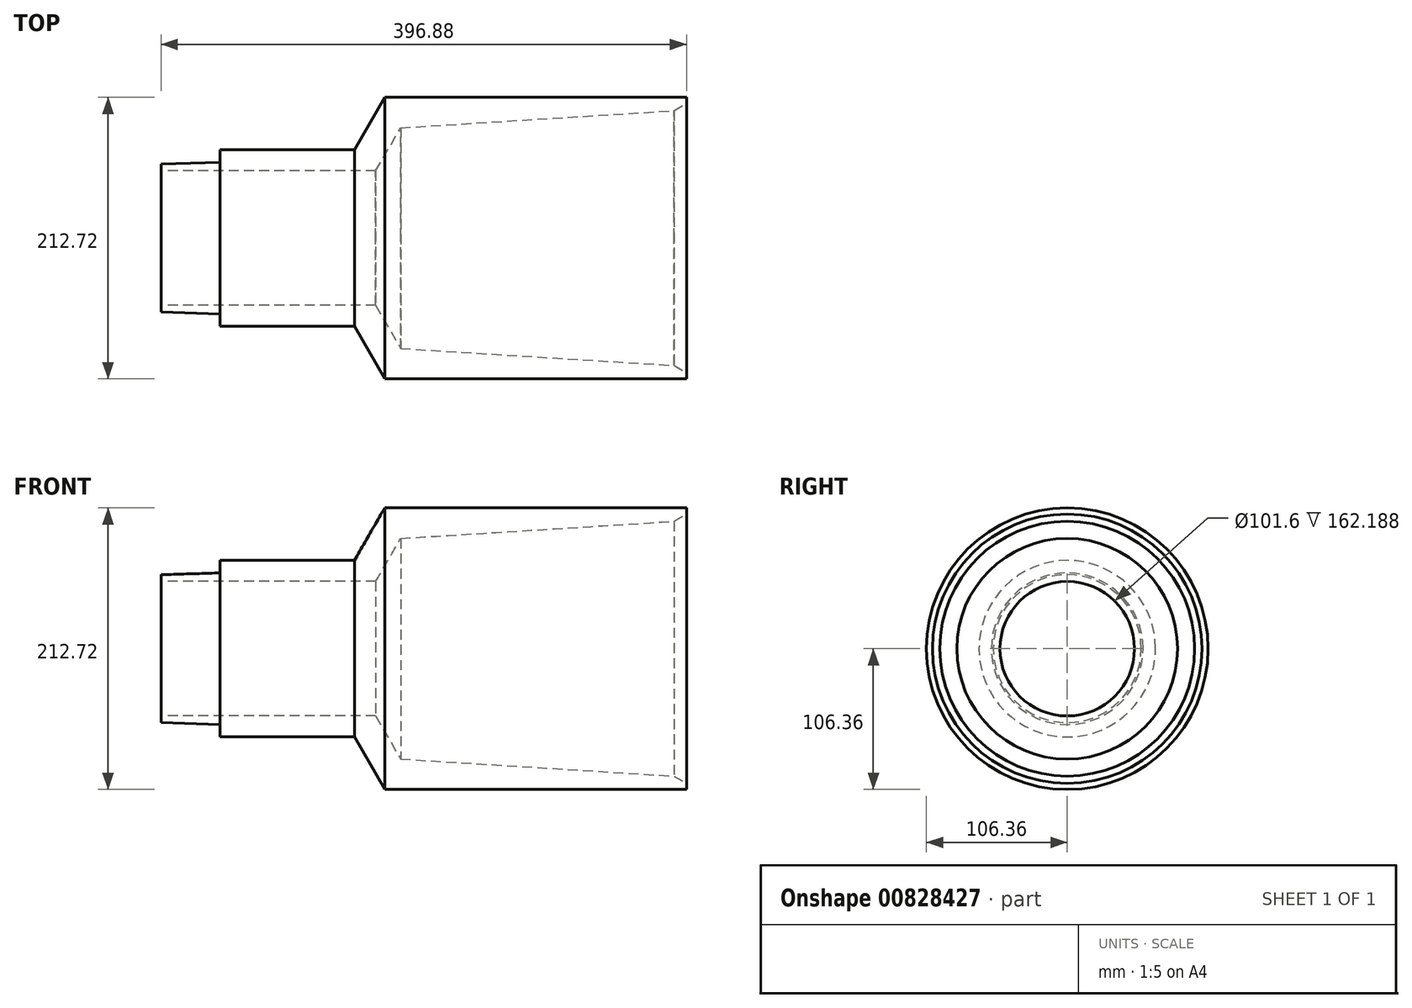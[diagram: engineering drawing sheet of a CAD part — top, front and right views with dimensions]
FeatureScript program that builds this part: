
annotation { "Feature Type Name" : "Feature", "Feature Type Description" : "" }
export const myFeature = defineFeature(function(context is Context, id is Id, definition is map)
    precondition{}
    {
        {
            var Q0;
            Q0=qCreatedBy(makeId("Front.planeOp"),FACE);
            var sketch = newSketch(context, id + "F0", { "sketchPlane" : qUnion([Q0])});
            skLineSegment(sketch, "E0", {"start": v(0, 50.8) * mm, "end": v(162.19, 50.8) * mm});
            skLineSegment(sketch, "E1", {"start": v(44.45, 66.68) * mm, "end": v(146.05, 66.68) * mm});
            skLineSegment(sketch, "E2", {"start": v(44.45, 66.68) * mm, "end": v(44.45, 57.28) * mm});
            skLineSegment(sketch, "E3", {"start": v(0, 55.89) * mm, "end": v(0, 50.8) * mm});
            skLineSegment(sketch, "E4", {"start": v(44.45, 57.28) * mm, "end": v(0, 55.89) * mm});
            skLineSegment(sketch, "E5", {"start": v(396.88, 106.36) * mm, "end": v(396.88, 101.74) * mm});
            skLineSegment(sketch, "E6", {"start": v(168.96, 106.36) * mm, "end": v(396.88, 106.36) * mm});
            skLineSegment(sketch, "E7", {"start": v(387.35, 96.24) * mm, "end": v(180.98, 83.34) * mm});
            skLineSegment(sketch, "E8", {"start": v(168.96, 106.36) * mm, "end": v(146.05, 66.68) * mm});
            skLineSegment(sketch, "E9", {"start": v(180.98, 83.34) * mm, "end": v(162.19, 50.8) * mm});
            skLineSegment(sketch, "E10", {"start": v(387.35, 96.24) * mm, "end": v(396.88, 101.74) * mm});
            skLineSegment(sketch, "E11", {"start": v(0, 0) * mm, "end": v(23.8, 0) * mm, "construction": true});
            skSolve(sketch);
        }
        {
            var Q0;
            Q0 = qSketchRegion(id + "F0", true);
            var Q1;
            Q1=sQuery(id+"F0.wireOp",EDGE,"E11");
            revolve(context, id + "F1", {"surfaceOperationType" : NewSurfaceOperationType.NEW, "entities" : qUnion([Q0]), "axis" : qUnion([Q1]), "revolveType" : RevolveType.FULL});
        }
    });
